# Revit family: RVT_MACOM_FTC1_2TC-3TC 12 23 B
name_source: partatom
category: Specialty Equipment
units: mm (PartAtom-declared; Revit-internal decimal feet)

## family parameters
Always vertical = Yes
Cut with Voids When Loaded = No
OmniClass Number = 23.40.40.14.17.24
OmniClass Title = Fryers
Part Type = Normal
Room Calculation Point = No
Round Connector Dimension = Use Diameter
Shared = No
Work Plane-Based = No

## types (2) — shared parameters
Cycle = 60 Hz
Default Elevation = 0,000 mm
Degree of Protection = IP 22
Depth = 785,000 mm
Description = FRITADEIRA ELETRICA MACOM COMERCIAL FULL 25 LITROS
Elec Connection Height = 59,000 mm
Electric Power = 16000 W
Height = 1208,000 mm
Manufacturer = MACOM
Oil Capacity = 25,0 L
Phase = 3
Show Clearances = Yes
URL = https://www.acosmacom.com.br
Volume = 0,36 m³
Weight = 51,00 kg
Width = 400,000 mm
Work Temperature = 80 °C - 180 ° C

## per-type parameters (varying)
| type | Operational Current | Volts |
| FTC1-2TC | 42 A | 220 V |
| FTC1-3TC | 24 A | 380 V |

note: column(s) folded — value = type name in every type: Model

## geometry (parser evidence)
native form markers: Sweep x10
no freeform markers — native parametric forms only
